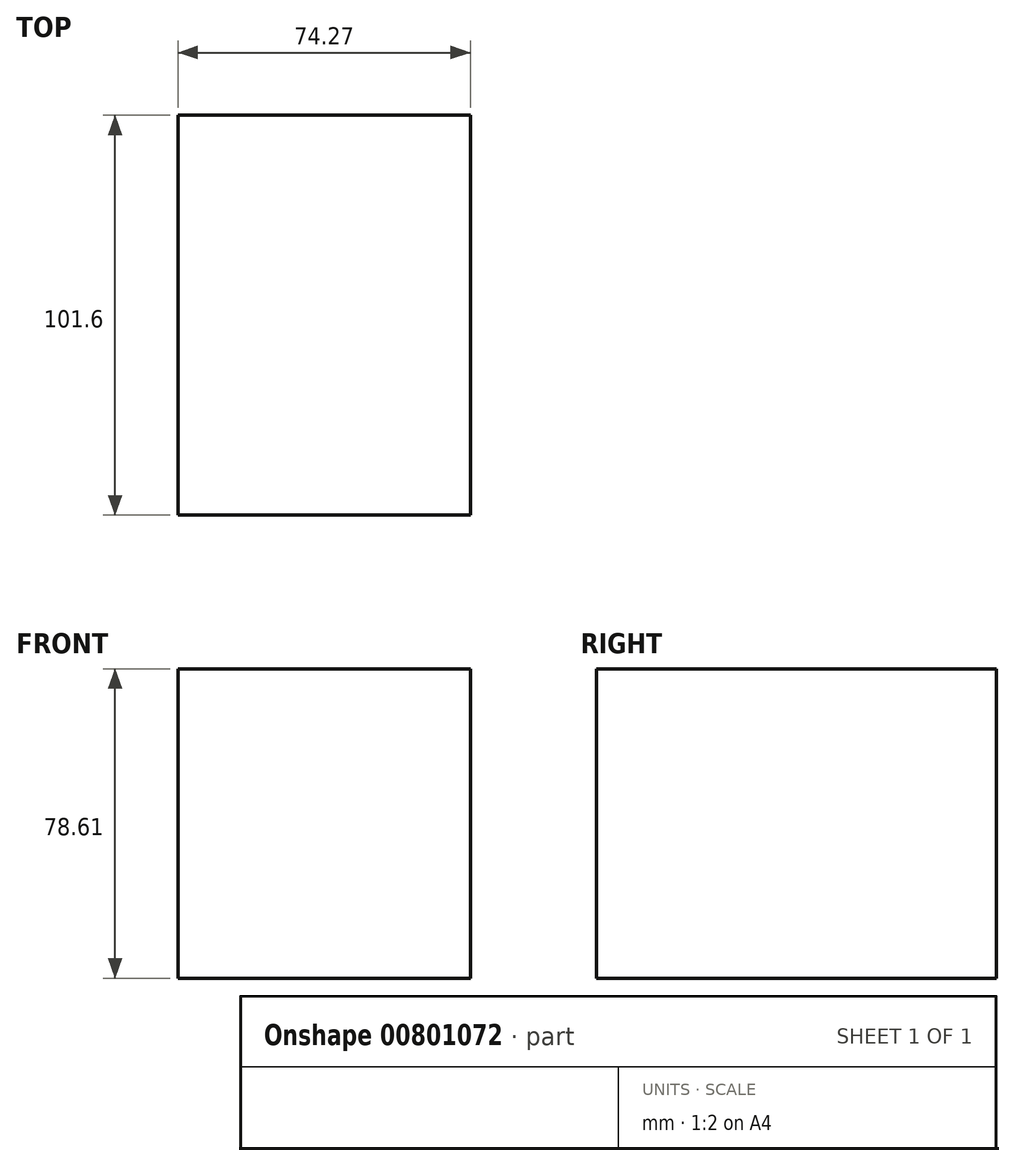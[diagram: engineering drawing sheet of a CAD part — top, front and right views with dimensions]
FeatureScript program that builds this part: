
annotation { "Feature Type Name" : "Feature", "Feature Type Description" : "" }
export const myFeature = defineFeature(function(context is Context, id is Id, definition is map)
    precondition{}
    {
        {
            var Q0;
            Q0=qCreatedBy(makeId("Front.planeOp"),FACE);
            var sketch = newSketch(context, id + "F0", { "sketchPlane" : qUnion([Q0])});
            skLineSegment(sketch, "E0", {"start": v(0, 0) * mm, "end": v(74.27, 0) * mm});
            skLineSegment(sketch, "E1", {"start": v(74.27, 0) * mm, "end": v(74.27, 78.61) * mm});
            skLineSegment(sketch, "E2", {"start": v(74.27, 78.61) * mm, "end": v(0, 78.61) * mm});
            skLineSegment(sketch, "E3", {"start": v(0, 78.61) * mm, "end": v(0, 0) * mm});
            skSolve(sketch);
        }
        {
            var Q0;
            Q0 = qSketchRegion(id + "F0", true);
            extrude(context, id + "F1", {"entities" : qUnion([Q0]), "depth" : 101.6 * mm, "offsetDistance" : 25.4 * mm});
        }
    });
